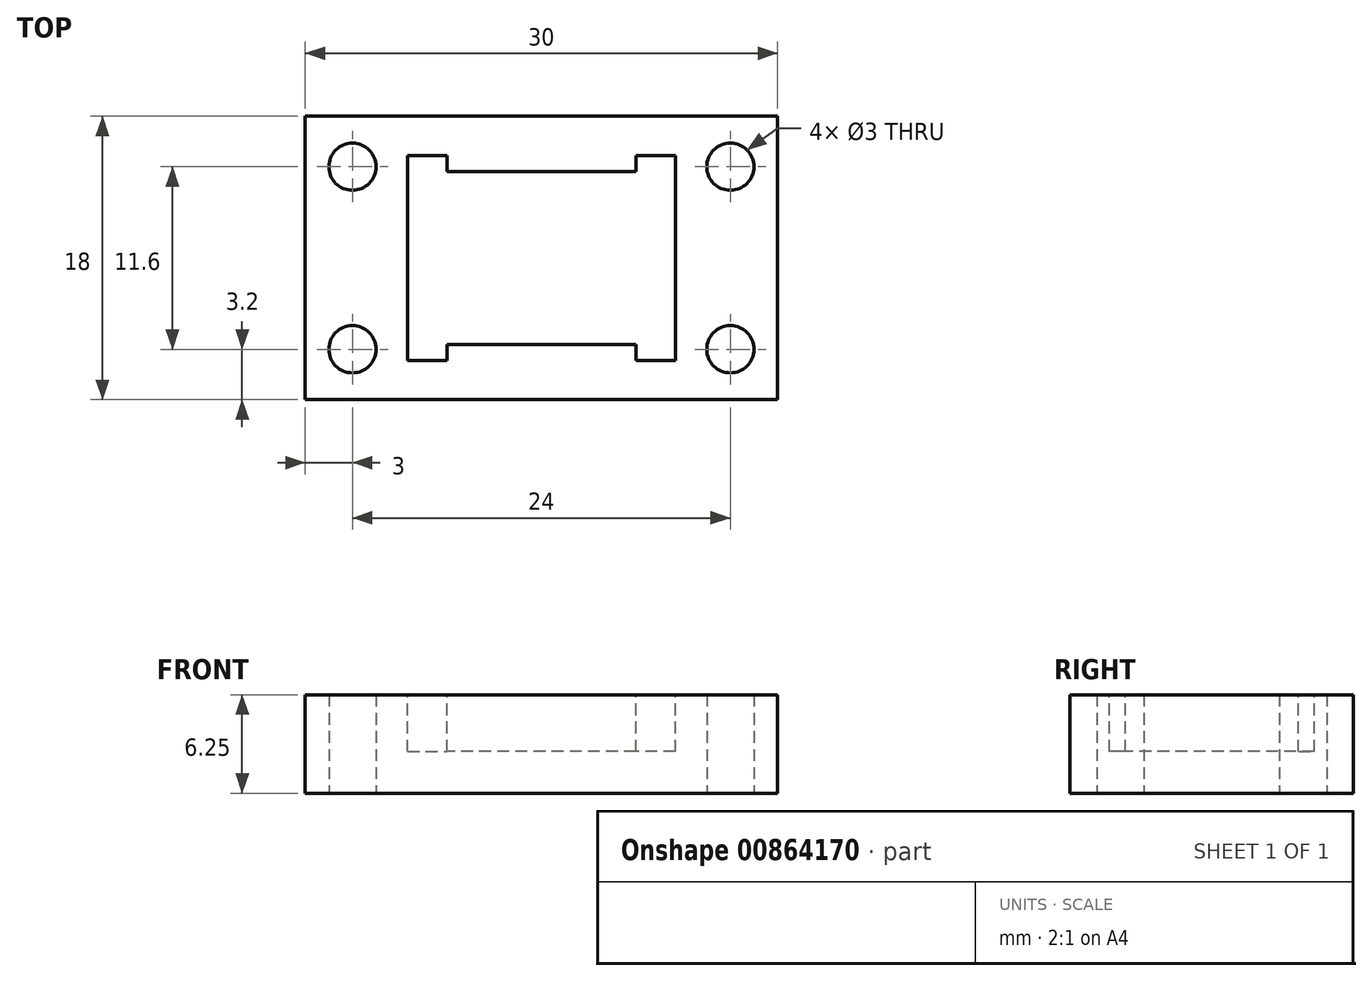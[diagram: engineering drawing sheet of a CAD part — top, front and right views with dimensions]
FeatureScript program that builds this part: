
annotation { "Feature Type Name" : "Feature", "Feature Type Description" : "" }
export const myFeature = defineFeature(function(context is Context, id is Id, definition is map)
    precondition{}
    {
        {
            var Q0;
            Q0=qCreatedBy(makeId("Top.planeOp"),FACE);
            var sketch = newSketch(context, id + "F0", { "sketchPlane" : qUnion([Q0])});
            skLineSegment(sketch, "E0.bottom", {"start": v(15, 9) * mm, "end": v(-15, 9) * mm});
            skLineSegment(sketch, "E0.top", {"start": v(15, -9) * mm, "end": v(-15, -9) * mm});
            skLineSegment(sketch, "E0.left", {"start": v(15, 9) * mm, "end": v(15, -9) * mm});
            skLineSegment(sketch, "E0.right", {"start": v(-15, 9) * mm, "end": v(-15, -9) * mm});
            skPoint(sketch, "E0.middle", {"position": v(0, 0) * mm});
            skLineSegment(sketch, "E1.bottom", {"start": v(12, 5.8) * mm, "end": v(-12, 5.8) * mm, "construction": true});
            skLineSegment(sketch, "E1.top", {"start": v(12, -5.8) * mm, "end": v(-12, -5.8) * mm, "construction": true});
            skLineSegment(sketch, "E1.left", {"start": v(12, 5.8) * mm, "end": v(12, -5.8) * mm, "construction": true});
            skLineSegment(sketch, "E1.right", {"start": v(-12, 5.8) * mm, "end": v(-12, -5.8) * mm, "construction": true});
            skCircle(sketch, "E2", {"center": v(-12, 5.8) * mm, "radius": 1.5 * mm});
            skCircle(sketch, "E3", {"center": v(12, 5.8) * mm, "radius": 1.5 * mm});
            skCircle(sketch, "E4", {"center": v(12, -5.8) * mm, "radius": 1.5 * mm});
            skCircle(sketch, "E5", {"center": v(-12, -5.8) * mm, "radius": 1.5 * mm});
            skSolve(sketch);
        }
        {
            var Q0;
            Q0 = qSketchRegion(id + "F0", true);
            extrude(context, id + "F1", {"entities" : qUnion([Q0]), "depth" : 6.25 * mm, "offsetDistance" : 25 * mm});
        }
        {
            var Q0;
            Q0=makeQuery(id+"F1.opExtrude","CAP_FACE",FACE,{"disambiguationData":[OSD([sQuery(id+"F0.wireOp",EDGE,"E0.bottom"),sQuery(id+"F0.wireOp",EDGE,"E0.top"),sQuery(id+"F0.wireOp",EDGE,"E0.left"),sQuery(id+"F0.wireOp",EDGE,"E0.right"),sQuery(id+"F0.wireOp",EDGE,"E2"),sQuery(id+"F0.wireOp",EDGE,"E3"),sQuery(id+"F0.wireOp",EDGE,"E4"),sQuery(id+"F0.wireOp",EDGE,"E5")])],"isStart":false});
            var sketch = newSketch(context, id + "F2", { "sketchPlane" : qUnion([Q0])});
            skLineSegment(sketch, "E6.bottom", {"start": v(8.5, 6.5) * mm, "end": v(-8.5, 6.5) * mm, "construction": true});
            skLineSegment(sketch, "E6.top", {"start": v(8.5, -6.5) * mm, "end": v(-8.5, -6.5) * mm, "construction": true});
            skLineSegment(sketch, "E6.left", {"start": v(8.5, 6.5) * mm, "end": v(8.5, -6.5) * mm});
            skLineSegment(sketch, "E6.right", {"start": v(-8.5, 6.5) * mm, "end": v(-8.5, -6.5) * mm});
            skPoint(sketch, "E6.middle", {"position": v(0, 0) * mm});
            skLineSegment(sketch, "E7", {"start": v(-8.5, 6.5) * mm, "end": v(-6, 6.5) * mm});
            skLineSegment(sketch, "E8", {"start": v(-6, 6.5) * mm, "end": v(-6, 5.5) * mm});
            skLineSegment(sketch, "E9", {"start": v(-6, 5.5) * mm, "end": v(6, 5.5) * mm});
            skLineSegment(sketch, "E10", {"start": v(6, 5.5) * mm, "end": v(6, 6.5) * mm});
            skLineSegment(sketch, "E11", {"start": v(6, 6.5) * mm, "end": v(8.5, 6.5) * mm});
            skLineSegment(sketch, "E12", {"start": v(8.5, -6.5) * mm, "end": v(6, -6.5) * mm});
            skLineSegment(sketch, "E13", {"start": v(6, -6.5) * mm, "end": v(6, -5.5) * mm});
            skLineSegment(sketch, "E14", {"start": v(6, -5.5) * mm, "end": v(-6, -5.5) * mm});
            skLineSegment(sketch, "E15", {"start": v(-6, -5.5) * mm, "end": v(-6, -6.5) * mm});
            skLineSegment(sketch, "E16", {"start": v(-6, -6.5) * mm, "end": v(-8.5, -6.5) * mm});
            skSolve(sketch);
        }
        {
            var Q0;
            Q0 = qSketchRegion(id + "F2", true);
            extrude(context, id + "F3", {"entities" : qUnion([Q0]), "operationType" : NewBodyOperationType.REMOVE, "oppositeDirection" : true, "depth" : 3.6 * mm, "offsetDistance" : 25 * mm});
        }
    });
